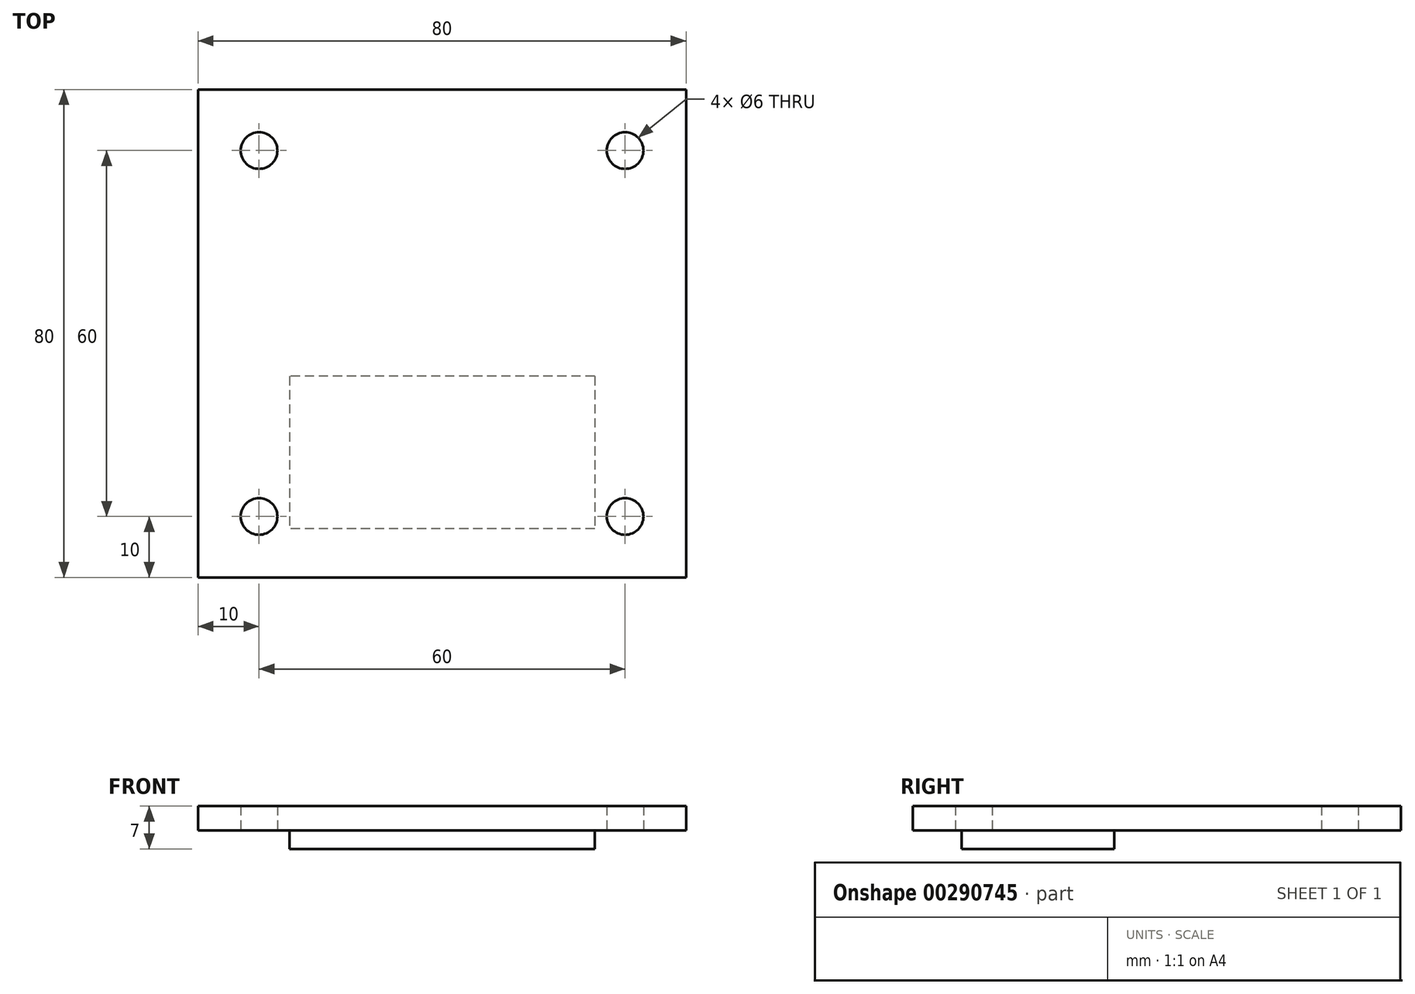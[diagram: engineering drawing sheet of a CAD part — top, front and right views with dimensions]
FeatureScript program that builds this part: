
annotation { "Feature Type Name" : "Feature", "Feature Type Description" : "" }
export const myFeature = defineFeature(function(context is Context, id is Id, definition is map)
    precondition{}
    {
        {
            var Q0;
            Q0=qCreatedBy(makeId("Top.planeOp"),FACE);
            var sketch = newSketch(context, id + "F0", { "sketchPlane" : qUnion([Q0])});
            skLineSegment(sketch, "E0.bottom", {"start": v(-40, -40) * mm, "end": v(40, -40) * mm});
            skLineSegment(sketch, "E0.top", {"start": v(-40, 40) * mm, "end": v(40, 40) * mm});
            skLineSegment(sketch, "E0.left", {"start": v(-40, -40) * mm, "end": v(-40, 40) * mm});
            skLineSegment(sketch, "E0.right", {"start": v(40, -40) * mm, "end": v(40, 40) * mm});
            skPoint(sketch, "E0.middle", {"position": v(0, 0) * mm});
            skPoint(sketch, "E1", {"position": v(-30, 30) * mm});
            skPoint(sketch, "E2", {"position": v(30, 30) * mm});
            skPoint(sketch, "E3", {"position": v(-30, -30) * mm});
            skPoint(sketch, "E4", {"position": v(30, -30) * mm});
            skSolve(sketch);
        }
        {
            var Q0;
            Q0=makeQuery(id+"F0.imprint","IMPRINT",FACE,{"disambiguationData":[TD([[makeQuery(id+"F0.imprint","IMPRINT",EDGE,{"derivedFrom":sQuery(id+"F0.wireOp",EDGE,"E0.bottom")}),1.0]])]});
            extrude(context, id + "F1", {"entities" : qUnion([Q0]), "depth" : 4 * mm});
        }
        {
            var Q0;
            Q0=makeQuery(id+"F1.opExtrude","CAP_FACE",FACE,{"disambiguationData":[OSD([sQuery(id+"F0.wireOp",EDGE,"E0.bottom"),sQuery(id+"F0.wireOp",EDGE,"E0.top"),sQuery(id+"F0.wireOp",EDGE,"E0.left"),sQuery(id+"F0.wireOp",EDGE,"E0.right")])],"isStart":true});
            var sketch = newSketch(context, id + "F2", { "sketchPlane" : qUnion([Q0])});
            skLineSegment(sketch, "E5.bottom", {"start": v(25, 7) * mm, "end": v(-25, 7) * mm});
            skLineSegment(sketch, "E5.top", {"start": v(25, 32) * mm, "end": v(-25, 32) * mm});
            skLineSegment(sketch, "E5.left", {"start": v(25, 7) * mm, "end": v(25, 32) * mm});
            skLineSegment(sketch, "E5.right", {"start": v(-25, 7) * mm, "end": v(-25, 32) * mm});
            skPoint(sketch, "E5.middle", {"position": v(0, 19.5) * mm});
            skSolve(sketch);
        }
        {
            var Q0;
            Q0=makeQuery(id+"F2.imprint","IMPRINT",FACE,{"disambiguationData":[TD([[makeQuery(id+"F2.imprint","IMPRINT",EDGE,{"derivedFrom":sQuery(id+"F2.wireOp",EDGE,"E5.bottom")}),-1.0]])]});
            extrude(context, id + "F3", {"entities" : qUnion([Q0]), "operationType" : NewBodyOperationType.ADD, "depth" : 3 * mm});
        }
        {
            var Q0;
            Q0=sQuery(id+"F0.wireOp",VERTEX,"E1");
            var Q1;
            Q1=sQuery(id+"F0.wireOp",VERTEX,"E2");
            var Q2;
            Q2=sQuery(id+"F0.wireOp",VERTEX,"E4");
            var Q3;
            Q3=sQuery(id+"F0.wireOp",VERTEX,"E3");
            var Q4;
            Q4=makeQuery(id+"F1.opExtrude","SWEPT_BODY",BODY,{"disambiguationData":[OSD([sQuery(id+"F0.wireOp",EDGE,"E0.bottom"),sQuery(id+"F0.wireOp",EDGE,"E0.top"),sQuery(id+"F0.wireOp",EDGE,"E0.left"),sQuery(id+"F0.wireOp",EDGE,"E0.right")])]});
            hole(context, id + "F4", {"style" : HoleStyle.SIMPLE, "endStyle" : HoleEndStyle.THROUGH, "oppositeDirection" : true, "holeDiameter" : 6 * mm, "tappedDepth" : 12 * mm, "tapClearance" : 3, "locations" : qUnion([Q0, Q1, Q2, Q3]), "scope" : qUnion([Q4])});
        }
    });
